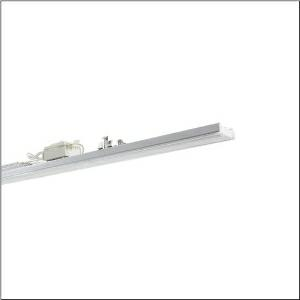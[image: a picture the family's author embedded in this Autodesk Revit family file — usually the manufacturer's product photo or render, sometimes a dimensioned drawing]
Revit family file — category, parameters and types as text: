
# Revit family: licross_21_recessed_mo_52tl19mn1axg
name_source: partatom
category: Lighting Fixtures
units: mm (PartAtom-declared; Revit-internal decimal feet)

## family parameters
Cut with Voids When Loaded = No
Host = Face
Light Source = No
Part Type = Normal
Room Calculation Point = No
Round Connector Dimension = Use Diameter
Shared = No

## types (1)
- --- (1 x LED, 10200 lm, 60.5 W, 3500K)
    Apparent Load = 61 VA
    CIE Flux Codes = 55 90 98 100 100
    Color Rendering = 80
    Color Temperature = 3500K
    Default Elevation = 1800 mm
    Description = Licross 21 Recessed MO, luminaire insert, of sheet steel, galvanised, coil coated, white, length: 1.500mm, width: 66mm, height: 67mm, LED rated luminous flux: 10.200lm, light colour: 835, SDCM (Standard Deviation of Colour Matching)MacAdam ≤ 3 SDCM (initial), control gear: ON/OFF Multilumen, with plug, 3-pole, with phase selection, mains connection: 220..240V, AC, 50/60Hz, rated input power: 60.5W, internal wiring halogen-free, primary light control with lens, of plastic, primary optical cover: cover, of PMMA, light emission: direct distribution, primary light characteristic: double asymmetric, protection rating (complete): IP40, insulation class (complete): insulation class I (protective earthing), certification: CE, ENEC, VDE, UKCA, protection symbol: D if used in an environment without relevant dust loads with corresponding accessories, impact resistance: IK06, permissible ambient temperature for indoor applications: -25..+35°C, corresponds to IFS (International Featured Standards) requirements for safety and quality in the food industry, reducing of maximum allowable ambient temperature of 5°C with ceiling mounting, LABS conformity tested according to VDMA 24364:2018-05, The light source and the operating device comply with the requirements of the Ecodesign Regulation (EU) 2019/2020 and are replaceable in accordance with this regulation, packaging unit: 1 piece
    Height = 58 mm
    Lamp = 1 x LED
    Lamp Light Flux = 10200 lm
    Lamp Power = 60.5 W
    Lamp count = 1
    Length = 1500 mm
    Luminous efficacy = 169 lm/W
    Manufacturer = Siteco
    ModVariant = No
    Model = 52TL19MN1AXG
    Mounting Place = Ceiling
    Mounting Type = Pendant
    Number of Poles = 1
    OnlyDefault = Yes
    Power Factor = 1
    Product Name = Licross 21 Recessed MO
    Product group = luminaire insert | ceiling pendant
    ProductGroupID = 901
    Protection Class = Protection class I
    Protection Degree = IP 40
    RLX_Detail_Level = 1
    RLX_Emergency_Light_Flux = 0 lm
    RLX_Emergency_Type = 0
    RLX_Emergency_Type_DB = No
    RlxData = <blob elided: 22533 chars, md5=546d5b6a>
    Socket = socket
    Standby Power = 0 W
    System Light Flux = 10200 lm
    System Power = 61 W
    Type Comments = factory setting: luminous flux: 100 % | (A | C | E) | 140 mA
    Type Image = l_1296930.jpg
    URL = http://relux.com
    VarID = @adj_075681
    Voltage = 0 V
    Weight = 0.00 kg
    Width = 66 mm

## geometry (parser evidence)
native form markers: Blend x4, Sweep x12
no freeform markers — native parametric forms only
